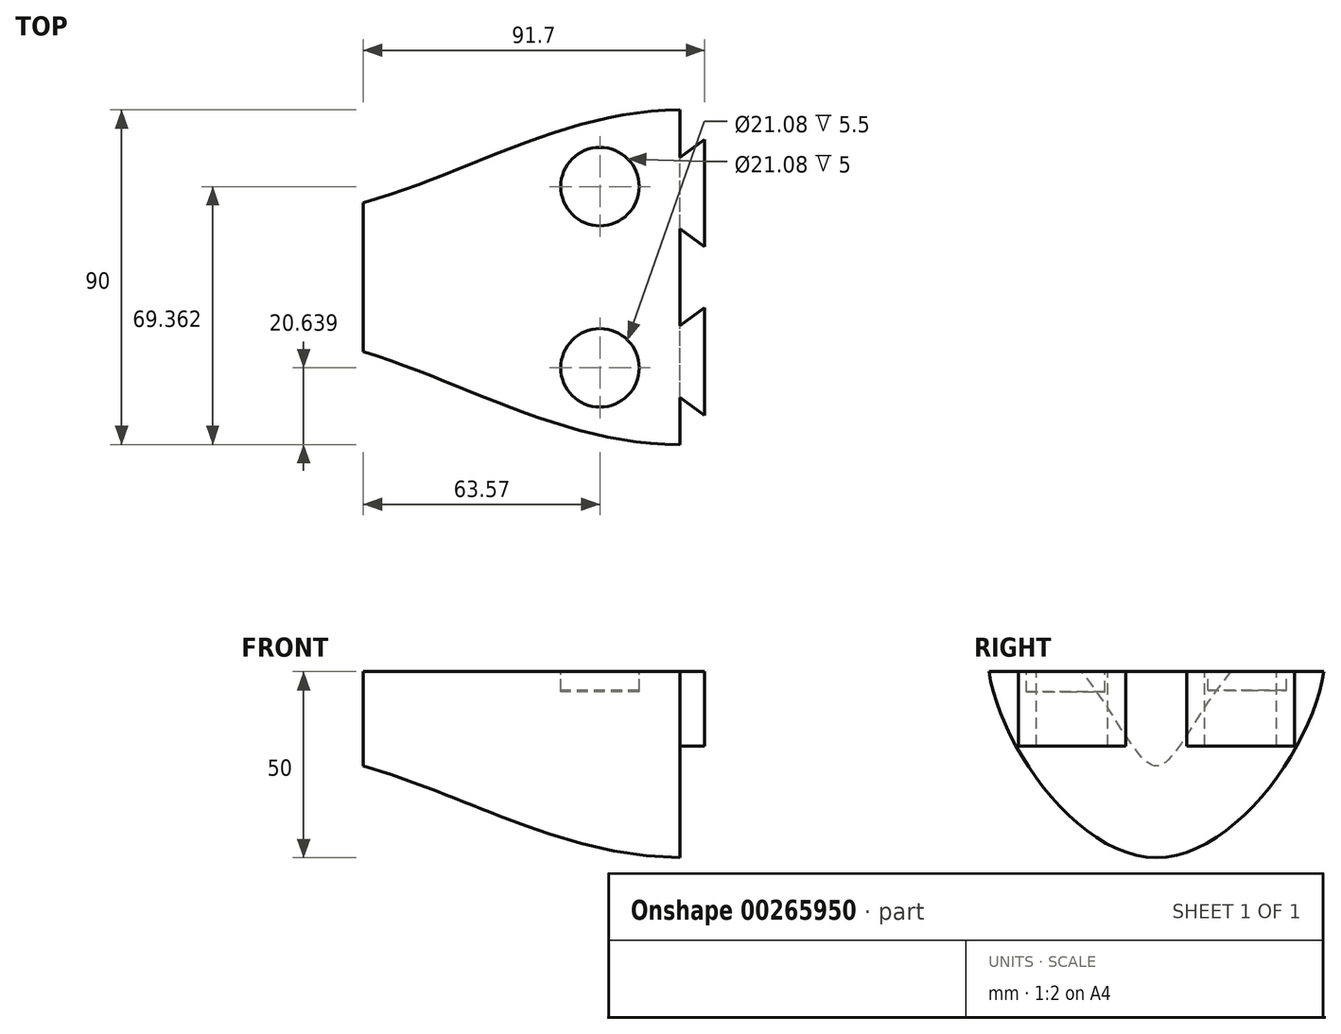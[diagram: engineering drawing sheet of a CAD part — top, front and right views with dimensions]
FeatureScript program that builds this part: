
annotation { "Feature Type Name" : "Feature", "Feature Type Description" : "" }
export const myFeature = defineFeature(function(context is Context, id is Id, definition is map)
    precondition{}
    {
        {
            var Q0;
            Q0=qCreatedBy(makeId("Right.planeOp"),FACE);
            cPlane(context, id + "F0", {"entities" : qUnion([Q0]), "cplaneType" : CPlaneType.OFFSET, "offset" : 85 * mm, "oppositeDirection" : true, "width" : 150 * mm, "height" : 150 * mm});
        }
        {
            var Q0;
            Q0=qCreatedBy(makeId("Right.planeOp"),FACE);
            var sketch = newSketch(context, id + "F1", { "sketchPlane" : qUnion([Q0])});
            skFitSpline(sketch, "E0", {"points": [v(-45, 0) * mm, v(0, -50) * mm, v(45, 0) * mm], "startDerivative": vector(18, -120) * mm, "endDerivative": vector(18, 120) * mm});
            skFitSpline(sketch, "E1", {"points": [v(-45, 0) * mm, v(45, 0) * mm], "startDerivative": vector(90, 0) * mm, "endDerivative": vector(90, 0) * mm});
            skSolve(sketch);
        }
        {
            var Q0;
            Q0=qCreatedBy(id+"F0.planeOp",FACE);
            var sketch = newSketch(context, id + "F2", { "sketchPlane" : qUnion([Q0])});
            skFitSpline(sketch, "E2", {"points": [v(20, 0) * mm, v(0, -25.4) * mm, v(-20, 0) * mm], "startDerivative": vector(-63.1, -76.02) * mm, "endDerivative": vector(-60.12, 76.36) * mm});
            skFitSpline(sketch, "E3", {"points": [v(20, 0) * mm, v(0, 0) * mm], "startDerivative": vector(-20, 0) * mm, "endDerivative": vector(-20, 0) * mm});
            skFitSpline(sketch, "E4", {"points": [v(0, 0) * mm, v(-20, 0) * mm], "startDerivative": vector(-20, 0) * mm, "endDerivative": vector(-20, 0) * mm});
            skSolve(sketch);
        }
        {
            var Q0;
            Q0=qCreatedBy(makeId("Top.planeOp"),FACE);
            var sketch = newSketch(context, id + "F3", { "sketchPlane" : qUnion([Q0])});
            skFitSpline(sketch, "E5", {"points": [v(0, -45) * mm, v(-85, -20) * mm], "startDerivative": vector(-91.42, 0) * mm, "endDerivative": vector(-84.8, 26.32) * mm});
            skFitSpline(sketch, "E6", {"points": [v(0, 45) * mm, v(-85, 20) * mm], "startDerivative": vector(-89.76, 0) * mm, "endDerivative": vector(-85.09, -24.34) * mm});
            skPoint(sketch, "E7", {"position": v(-30.18, 0) * mm});
            skSolve(sketch);
        }
        {
            var Q0;
            Q0=qCreatedBy(makeId("Front.planeOp"),FACE);
            var sketch = newSketch(context, id + "F4", { "sketchPlane" : qUnion([Q0])});
            skFitSpline(sketch, "E8", {"points": [v(-85, -25.4) * mm, v(0, -50) * mm], "startDerivative": vector(85.69, -24.77) * mm, "endDerivative": vector(91.22, 0) * mm});
            skSolve(sketch);
        }
        {
            var Q0;
            Q0=makeQuery(id+"F1.imprint","IMPRINT",FACE,{"disambiguationData":[TD([[makeQuery(id+"F1.imprint","IMPRINT",EDGE,{"derivedFrom":sQuery(id+"F1.wireOp",EDGE,"E0")}),1.0]])]});
            var Q1;
            Q1=makeQuery(id+"F2.imprint","IMPRINT",FACE,{"disambiguationData":[TD([[makeQuery(id+"F2.imprint","IMPRINT",EDGE,{"derivedFrom":sQuery(id+"F2.wireOp",EDGE,"E2")}),-1.0]])]});
            var Q2;
            Q2=sQuery(id+"F3.wireOp",EDGE,"E6");
            var Q3;
            Q3=sQuery(id+"F3.wireOp",EDGE,"E5");
            var Q4;
            Q4=sQuery(id+"F4.wireOp",EDGE,"E8");
            loft(context, id + "F5", {"addGuides" : true, "sheetProfilesArray" : [{ "sheetProfileEntities" : qUnion([Q0]) }, { "sheetProfileEntities" : qUnion([Q1]) }], "guidesArray" : [{ "guideEntities" : qUnion([Q2]), "guideDerivativeType" : LoftGuideDerivativeType.DEFAULT, "guideDerivativeMagnitude" : 1 }, { "guideEntities" : qUnion([Q3]), "guideDerivativeType" : LoftGuideDerivativeType.DEFAULT, "guideDerivativeMagnitude" : 1 }, { "guideEntities" : qUnion([Q4]), "guideDerivativeType" : LoftGuideDerivativeType.DEFAULT, "guideDerivativeMagnitude" : 1 }]});
        }
        {
            var Q0;
            Q0=makeQuery(id+"F5.opLoft","SWEPT_FACE",FACE,{"disambiguationData":[OSD([sQuery(id+"F1.wireOp",EDGE,"E1"),sQuery(id+"F2.wireOp",EDGE,"E3"),sQuery(id+"F2.wireOp",EDGE,"E4"),sQuery(id+"F3.wireOp",EDGE,"E5")])]});
            var sketch = newSketch(context, id + "F6", { "sketchPlane" : qUnion([Q0])});
            skLineSegment(sketch, "E9", {"start": v(0, 32.26) * mm, "end": v(6.7, 37.08) * mm});
            skLineSegment(sketch, "E10", {"start": v(6.7, 37.08) * mm, "end": v(6.7, 8.19) * mm});
            skLineSegment(sketch, "E11", {"start": v(6.7, 8.19) * mm, "end": v(0, 13) * mm});
            skSolve(sketch);
        }
        {
            var Q0;
            {var subQ0=sQuery(id+"F6.wireOp",EDGE,"E9");Q0=makeQuery(id+"F6.imprint","IMPRINT",FACE,{"disambiguationData":[TD([[makeQuery(id+"F6.imprint","IMPRINT",EDGE,{"derivedFrom":subQ0}),-1.0]])]});}
            extrude(context, id + "F7", {"entities" : qUnion([Q0]), "operationType" : NewBodyOperationType.ADD, "oppositeDirection" : true, "depth" : 20 * mm});
        }
        {
            var Q0;
            {var subQ0=sQuery(id+"F3.wireOp",EDGE,"E5");var subQ1=sQuery(id+"F1.wireOp",EDGE,"E1");Q0=makeQuery(id+"F7.boolean.opBoolean","MERGE",FACE,{"derivedFrom":[makeQuery(id+"F5.opLoft","SWEPT_FACE",FACE,{"disambiguationData":[OSD([subQ1,sQuery(id+"F2.wireOp",EDGE,"E3"),sQuery(id+"F2.wireOp",EDGE,"E4"),subQ0])]}),makeQuery(id+"F7.opExtrude","CAP_FACE",FACE,{"disambiguationData":[OSD([subQ1,subQ0,sQuery(id+"F6.wireOp",EDGE,"E9"),sQuery(id+"F6.wireOp",EDGE,"E10"),sQuery(id+"F6.wireOp",EDGE,"E11")])],"isStart":true})]});}
            var sketch = newSketch(context, id + "F8", { "sketchPlane" : qUnion([Q0])});
            skLineSegment(sketch, "E12", {"start": v(0, -13.03) * mm, "end": v(6.7, -8.21) * mm});
            skLineSegment(sketch, "E13", {"start": v(6.7, -8.21) * mm, "end": v(6.7, -37.1) * mm});
            skLineSegment(sketch, "E14", {"start": v(6.7, -37.1) * mm, "end": v(0, -32.3) * mm});
            skSolve(sketch);
        }
        {
            var Q0;
            {var subQ0=sQuery(id+"F8.wireOp",EDGE,"E12");Q0=makeQuery(id+"F8.imprint","IMPRINT",FACE,{"disambiguationData":[TD([[makeQuery(id+"F8.imprint","IMPRINT",EDGE,{"derivedFrom":subQ0}),-1.0]])]});}
            extrude(context, id + "F9", {"entities" : qUnion([Q0]), "operationType" : NewBodyOperationType.ADD, "oppositeDirection" : true, "depth" : 20 * mm});
        }
        {
            var Q0;
            {var subQ0=sQuery(id+"F3.wireOp",EDGE,"E5");var subQ1=sQuery(id+"F1.wireOp",EDGE,"E1");Q0=makeQuery(id+"F9.boolean.opBoolean","MERGE",FACE,{"derivedFrom":[makeQuery(id+"F7.boolean.opBoolean","MERGE",FACE,{"derivedFrom":[makeQuery(id+"F5.opLoft","SWEPT_FACE",FACE,{"disambiguationData":[OSD([subQ1,sQuery(id+"F2.wireOp",EDGE,"E3"),sQuery(id+"F2.wireOp",EDGE,"E4"),subQ0])]}),makeQuery(id+"F7.opExtrude","CAP_FACE",FACE,{"disambiguationData":[OSD([subQ1,subQ0,sQuery(id+"F6.wireOp",EDGE,"E9"),sQuery(id+"F6.wireOp",EDGE,"E10"),sQuery(id+"F6.wireOp",EDGE,"E11")])],"isStart":true})]}),makeQuery(id+"F9.opExtrude","CAP_FACE",FACE,{"disambiguationData":[OSD([subQ1,subQ0,sQuery(id+"F8.wireOp",EDGE,"E12"),sQuery(id+"F8.wireOp",EDGE,"E13"),sQuery(id+"F8.wireOp",EDGE,"E14")])],"isStart":true})]});}
            var sketch = newSketch(context, id + "F10", { "sketchPlane" : qUnion([Q0])});
            skCircle(sketch, "E15", {"center": v(-21.43, -24.36) * mm, "radius": 10.54 * mm});
            skCircle(sketch, "E16.MirrorC", {"center": v(-21.43, 24.36) * mm, "radius": 10.54 * mm});
            skSolve(sketch);
        }
        {
            var Q0;
            Q0=makeQuery(id+"F10.imprint","IMPRINT",FACE,{"disambiguationData":[TD([[makeQuery(id+"F10.imprint","IMPRINT",EDGE,{"derivedFrom":sQuery(id+"F10.wireOp",EDGE,"E15")}),1.0]])]});
            extrude(context, id + "F11", {"entities" : qUnion([Q0]), "operationType" : NewBodyOperationType.REMOVE, "depth" : 5.5 * mm});
        }
        {
            var Q0;
            Q0=makeQuery(id+"F10.imprint","IMPRINT",FACE,{"disambiguationData":[TD([[makeQuery(id+"F10.imprint","IMPRINT",EDGE,{"derivedFrom":sQuery(id+"F10.wireOp",EDGE,"E15")}),1.0]])]});
            extrude(context, id + "F12", {"entities" : qUnion([Q0]), "operationType" : NewBodyOperationType.REMOVE, "oppositeDirection" : true, "depth" : 5.5 * mm});
        }
        {
            var Q0;
            Q0 = qSketchRegion(id + "F10", true);
            extrude(context, id + "F13", {"entities" : qUnion([Q0]), "operationType" : NewBodyOperationType.REMOVE, "oppositeDirection" : true, "depth" : 5 * mm});
        }
    });
